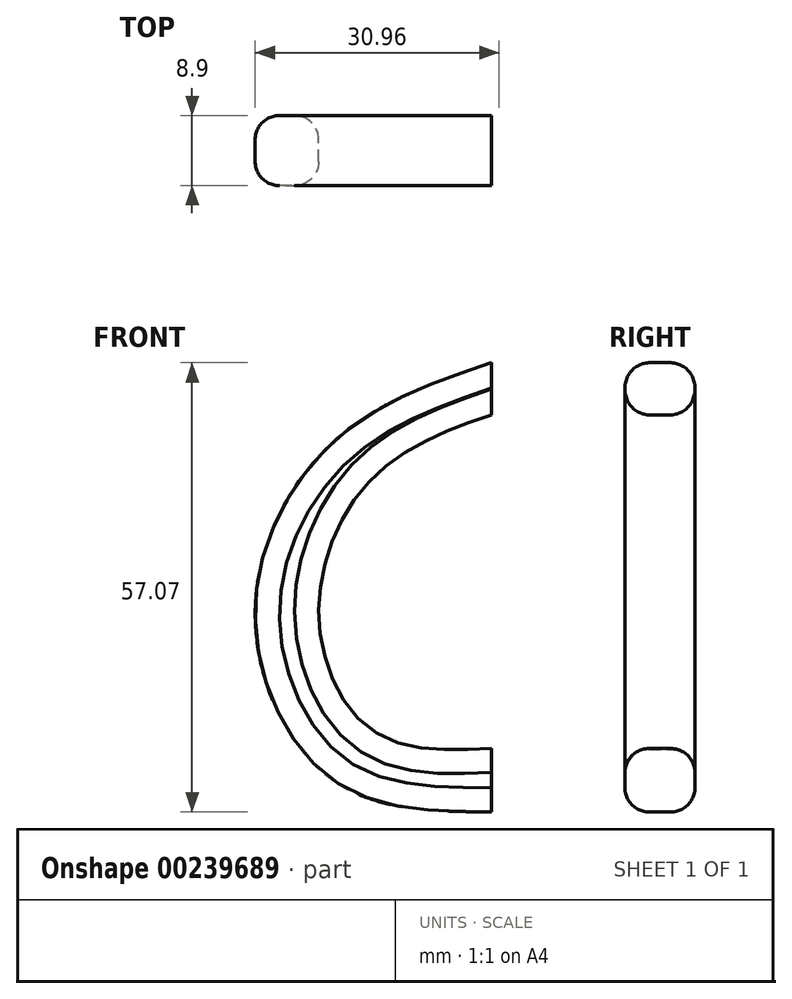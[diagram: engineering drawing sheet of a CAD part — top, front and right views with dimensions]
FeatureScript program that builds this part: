
annotation { "Feature Type Name" : "Feature", "Feature Type Description" : "" }
export const myFeature = defineFeature(function(context is Context, id is Id, definition is map)
    precondition{}
    {
        {
            var Q0;
            Q0=qCreatedBy(makeId("Front.planeOp"),FACE);
            var sketch = newSketch(context, id + "F0", { "sketchPlane" : qUnion([Q0])});
            skFitSpline(sketch, "E0", {"points": [v(0, 24.8) * mm, v(-14.68, 17.16) * mm, v(-21.91, 0) * mm, v(-15.1, -15.3) * mm, v(0, -17.57) * mm], "startDerivative": vector(-64.11, -22.5) * mm, "endDerivative": vector(69.53, 3.12) * mm});
            skFitSpline(sketch, "E1", {"points": [v(0, 31.43) * mm, v(-19.64, 21.71) * mm, v(-29.98, 0) * mm, v(-20.26, -21.5) * mm, v(0, -25.64) * mm], "startDerivative": vector(-85.43, -28.93) * mm, "endDerivative": vector(92.03, -0.72) * mm});
            skLineSegment(sketch, "E2", {"start": v(0, 31.43) * mm, "end": v(0, 24.8) * mm});
            skLineSegment(sketch, "E3", {"start": v(0, -17.57) * mm, "end": v(0, -25.64) * mm});
            skSolve(sketch);
        }
        {
            var Q0;
            Q0 = qSketchRegion(id + "F0", true);
            extrude(context, id + "F1", {"entities" : qUnion([Q0]), "endBound" : BoundingType.SYMMETRIC, "depth" : 8.9 * mm});
        }
        {
            var Q0;
            Q0=makeQuery(id+"F1.opExtrude","CAP_EDGE",EDGE,{"disambiguationData":[OSD([sQuery(id+"F0.wireOp",EDGE,"E1")])],"isStart":false});
            var Q1;
            Q1=makeQuery(id+"F1.opExtrude","CAP_EDGE",EDGE,{"disambiguationData":[OSD([sQuery(id+"F0.wireOp",EDGE,"E1")])],"isStart":true});
            var Q2;
            Q2=makeQuery(id+"F1.opExtrude","CAP_EDGE",EDGE,{"disambiguationData":[OSD([sQuery(id+"F0.wireOp",EDGE,"E0")])],"isStart":true});
            var Q3;
            Q3=makeQuery(id+"F1.opExtrude","CAP_EDGE",EDGE,{"disambiguationData":[OSD([sQuery(id+"F0.wireOp",EDGE,"E0")])],"isStart":false});
            fillet(context, id + "F2", {"entities" : qUnion([Q0, Q1, Q2, Q3]), "radius" : 3.07 * mm, "tangentPropagation" : true, "allowEdgeOverflow" : false});
        }
    });
